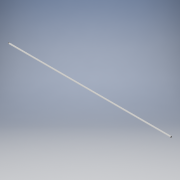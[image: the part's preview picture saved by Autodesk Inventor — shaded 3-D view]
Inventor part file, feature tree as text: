
AUTODESK INVENTOR PART (.ipt)
format: ipt  version: 2019 (Build 230136000, 136)  size: 90,112 bytes
history: native  units: in
note: dims shown in document units (in); Inventor stores cm internally (conversion verified against a paired STEP export)
features: extrude x1, sketch x1
ambient origin geometry x8: Origin, YZ Plane, XZ Plane, XY Plane, X Axis, Y Axis, Z Axis, Center Point
bodies: Solid1 (feature_tree)
feature tree (2):
  extrude  "Extrusion1"  Depth=39.3701in TaperAngle=0.0deg
  sketch  "Sketch1"  dims[d0=0.315in d1=39.3701in d2=0.0in]
